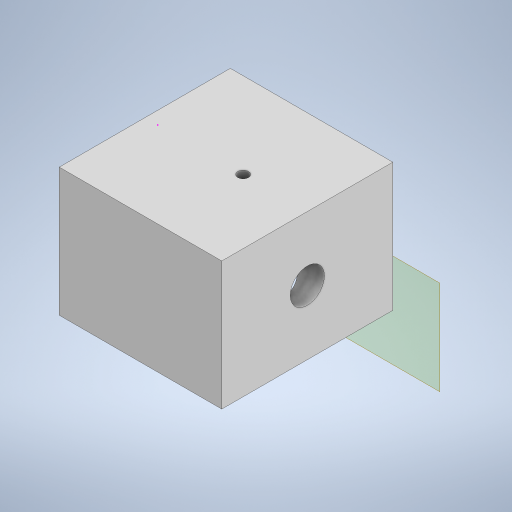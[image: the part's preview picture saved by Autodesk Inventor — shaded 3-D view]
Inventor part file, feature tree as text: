
AUTODESK INVENTOR PART (.ipt)
format: ipt  version: 2023 (Build 270158000, 158)  size: 278,016 bytes
history: native  units: mm
features: sketch x8, plane x6, extrude x6
ambient origin geometry x8: Origin, YZ Plane, XZ Plane, XY Plane, X Axis, Y Axis, Z Axis, Center Point
bodies: Body1 (feature_tree)
feature tree (20):
  plane  "Work Plane13"
  extrude  "Extrusion34"  Depth=40.0mm
  sketch  "Sketch46"  dims[d144=30.0mm d145=0.0mm d146=36.0mm]
  plane  "Work Plane11"
  extrude  "Extrusion35"  Depth=36.0mm
  sketch  "Sketch48"  dims[d150=0.0mm d151=0.0mm d156=20.0mm]
  extrude  "Extrusion36"  Depth=2.5mm
  plane  "Work Plane7"
  extrude  "Extrusion38"  Depth=20.0mm
  plane  "Work Plane4"
  extrude  "Extrusion39"  Depth=15.0mm TaperAngle=0.0deg
  plane  "Work Plane1"
  plane  "Work Plane6"
  extrude  "Extrusion42"  Depth=4.0mm
  sketch  "Sketch45"  dims[d142=38.0mm d143=40.0mm]
  sketch  "Sketch47"  dims[d147=30.0mm d148=-2.617994mm d149=2.5mm]
  sketch  "Sketch49"  dims[d157=15.0mm d158=15.0mm d159=0.0mm]
  sketch  "Sketch58"  dims[d160=4.0mm d161=20.0mm]
  sketch  "Sketch59"  dims[d162=35.0mm d163=0.0mm]
  sketch  "Sketch62"  dims[d172=8.0mm d173=0.0mm d174=0.0mm d49=0.5mm d50=0.872665mm d51=0.5mm d52=0.872665mm d130=0.5mm d131=0.872665mm d132=0.5mm d133=0.872665mm]
